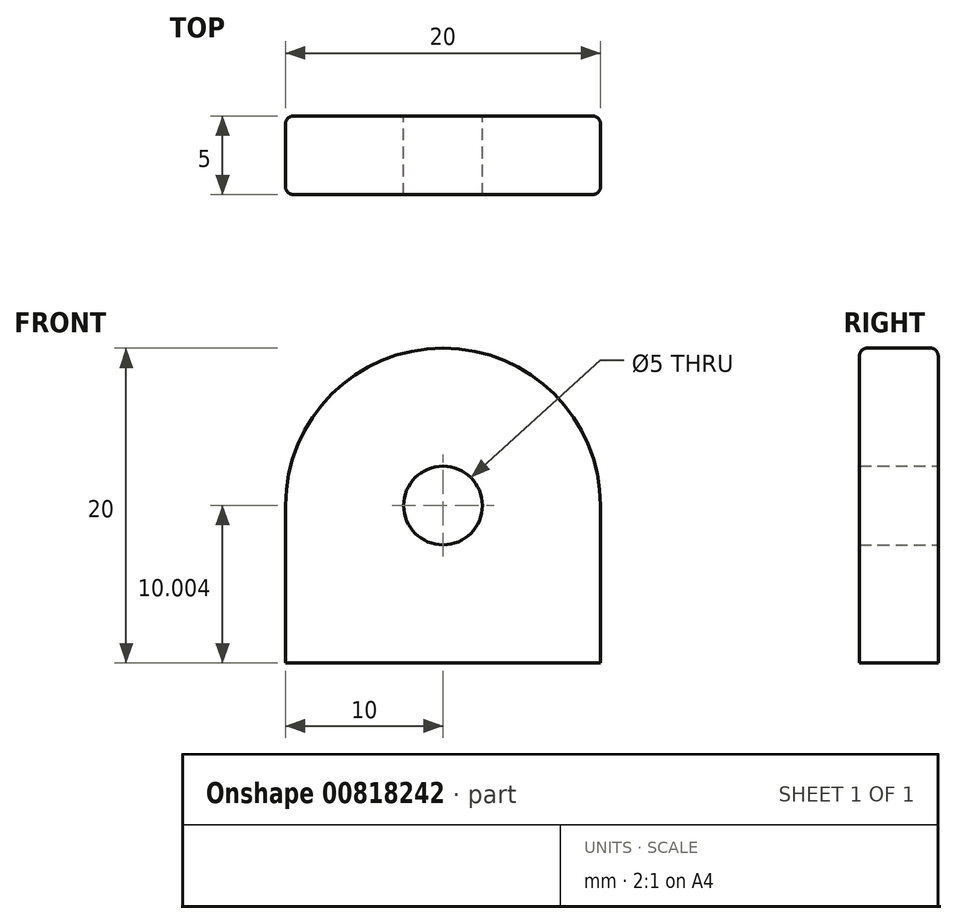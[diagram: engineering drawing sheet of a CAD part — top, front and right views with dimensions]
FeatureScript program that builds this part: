
annotation { "Feature Type Name" : "Feature", "Feature Type Description" : "" }
export const myFeature = defineFeature(function(context is Context, id is Id, definition is map)
    precondition{}
    {
        {
            var Q0;
            Q0=qCreatedBy(makeId("Front.planeOp"),FACE);
            var sketch = newSketch(context, id + "F0", { "sketchPlane" : qUnion([Q0])});
            skLineSegment(sketch, "E0", {"start": v(10, 12.1) * mm, "end": v(10, 22.1) * mm});
            skLineSegment(sketch, "E1", {"start": v(-10, 12.1) * mm, "end": v(-10, 22.1) * mm});
            skArc(sketch, "E2", {"start": v(10, 22.1) * mm, "mid": v(0, 32.1) * mm, "end": v(-10, 22.1) * mm});
            skLineSegment(sketch, "E3", {"start": v(-10, 12.1) * mm, "end": v(10, 12.1) * mm});
            skCircle(sketch, "E4", {"center": v(0, 22.1) * mm, "radius": 2.5 * mm});
            skSolve(sketch);
        }
        {
            var Q0;
            Q0=makeQuery(id+"F0.imprint","IMPRINT",FACE,{"disambiguationData":[TD([[makeQuery(id+"F0.imprint","IMPRINT",EDGE,{"derivedFrom":sQuery(id+"F0.wireOp",EDGE,"E0")}),1.0]])]});
            extrude(context, id + "F1", {"entities" : qUnion([Q0]), "depth" : 5 * mm, "offsetDistance" : 25 * mm});
        }
        {
            var Q0;
            Q0=makeQuery(id+"F1.opExtrude","CAP_EDGE",EDGE,{"disambiguationData":[OSD([sQuery(id+"F0.wireOp",EDGE,"E2")])],"isStart":false});
            var Q1;
            Q1=makeQuery(id+"F1.opExtrude","CAP_EDGE",EDGE,{"disambiguationData":[OSD([sQuery(id+"F0.wireOp",EDGE,"E0")])],"isStart":true});
            fillet(context, id + "F2", {"entities" : qUnion([Q0, Q1]), "radius" : 0.5 * mm, "tangentPropagation" : true, "allowEdgeOverflow" : false});
        }
    });
